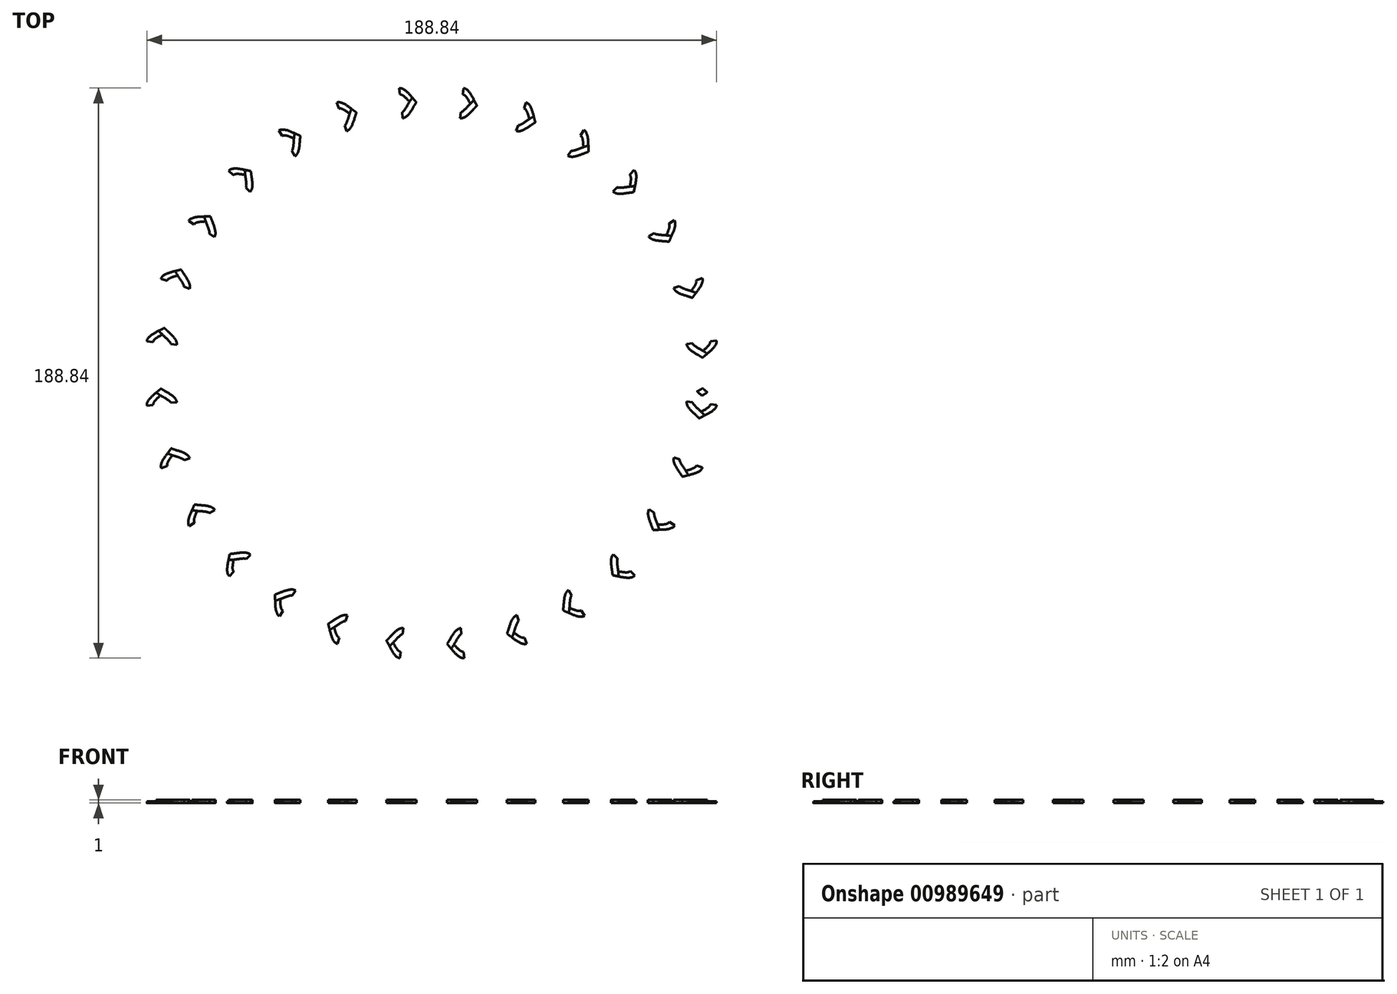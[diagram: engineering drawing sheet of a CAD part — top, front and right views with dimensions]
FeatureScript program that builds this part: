
annotation { "Feature Type Name" : "Feature", "Feature Type Description" : "" }
export const myFeature = defineFeature(function(context is Context, id is Id, definition is map)
    precondition{}
    {
        {
            var Q0;
            Q0=qCreatedBy(makeId("Top.planeOp"),FACE);
            var sketch = newSketch(context, id + "F0", { "sketchPlane" : qUnion([Q0])});
            skCircle(sketch, "E0", {"center": v(0, 0) * mm, "radius": 90 * mm, "construction": true});
            skLineSegment(sketch, "E1", {"start": v(0, 0) * mm, "end": v(90, 0) * mm, "construction": true});
            skLineSegment(sketch, "E2", {"start": v(89.42, 10.18) * mm, "end": v(90, 0) * mm, "construction": true});
            skLineSegment(sketch, "E3", {"start": v(0, 0) * mm, "end": v(89.42, 10.18) * mm, "construction": true});
            skLineSegment(sketch, "E4", {"start": v(90, 0) * mm, "end": v(89.44, -9.98) * mm, "construction": true});
            skLineSegment(sketch, "E5", {"start": v(0, 0) * mm, "end": v(89.44, -9.98) * mm, "construction": true});
            skLineSegment(sketch, "E6", {"start": v(90, 0) * mm, "end": v(85, 0) * mm});
            skLineSegment(sketch, "E7", {"start": v(85, 0) * mm, "end": v(87, 0) * mm});
            skLineSegment(sketch, "E8", {"start": v(90, 0) * mm, "end": v(95, 0) * mm});
            skLineSegment(sketch, "E9", {"start": v(95, 0) * mm, "end": v(93, 0) * mm});
            skLineSegment(sketch, "E10", {"start": v(89.42, 10.18) * mm, "end": v(84.45, 9.62) * mm});
            skLineSegment(sketch, "E11", {"start": v(84.45, 9.62) * mm, "end": v(86.44, 9.84) * mm});
            skLineSegment(sketch, "E12", {"start": v(86.44, 9.84) * mm, "end": v(86.67, 7.86) * mm, "construction": true});
            skLineSegment(sketch, "E13", {"start": v(84.45, 9.62) * mm, "end": v(84.68, 7.63) * mm, "construction": true});
            skLineSegment(sketch, "E14", {"start": v(89.42, 10.18) * mm, "end": v(94.39, 10.75) * mm});
            skLineSegment(sketch, "E15", {"start": v(94.39, 10.75) * mm, "end": v(92.28, 10.5) * mm});
            skLineSegment(sketch, "E16", {"start": v(92.28, 10.5) * mm, "end": v(92.5, 8.52) * mm, "construction": true});
            skLineSegment(sketch, "E17", {"start": v(94.39, 10.75) * mm, "end": v(94.62, 8.76) * mm, "construction": true});
            skLineSegment(sketch, "E18", {"start": v(87, 0) * mm, "end": v(87, 2) * mm, "construction": true});
            skLineSegment(sketch, "E19", {"start": v(93, 0) * mm, "end": v(93, 2) * mm, "construction": true});
            skLineSegment(sketch, "E20", {"start": v(90, 0) * mm, "end": v(89.71, 5.1) * mm, "construction": true});
            skFitSpline(sketch, "E21", {"points": [v(94.39, 10.75) * mm, v(89.71, 5.1) * mm, v(87, 0) * mm], "startDerivative": vector(1.28, -11.25) * mm, "endDerivative": vector(0, -12.77) * mm});
            skFitSpline(sketch, "E22", {"points": [v(84.45, 9.62) * mm, v(89.71, 5.1) * mm, v(93, 0) * mm], "startDerivative": vector(1.31, -11.53) * mm, "endDerivative": vector(0, -12.42) * mm});
            skFitSpline(sketch, "E23.0", {"points": [v(86.44, 9.84) * mm, v(86.44, 9.83) * mm, v(86.45, 9.8) * mm, v(86.56, 9.6) * mm, v(86.87, 9.27) * mm, v(87.4, 8.87) * mm, v(88.07, 8.43) * mm, v(88.86, 7.97) * mm, v(89.72, 7.47) * mm, v(90.46, 7) * mm, v(91.05, 6.6) * mm, v(91.63, 6.17) * mm, v(92.3, 5.6) * mm, v(93.04, 4.85) * mm, v(93.91, 3.76) * mm, v(94.74, 2.2) * mm, v(95, 0.74) * mm, v(95, 0) * mm]});
            skLineSegment(sketch, "E24", {"start": v(92.4, 10.52) * mm, "end": v(92.4, 10.5) * mm});
            skFitSpline(sketch, "E25", {"points": [v(85, 0) * mm, v(89.6, 7.15) * mm, v(92.28, 10.5) * mm], "startDerivative": vector(-0.2, 13.78) * mm, "endDerivative": vector(-0.82, 7.17) * mm});
            skLineSegment(sketch, "E26", {"start": v(89.44, -9.98) * mm, "end": v(84.48, -9.43) * mm});
            skLineSegment(sketch, "E27", {"start": v(84.48, -9.43) * mm, "end": v(86.46, -9.65) * mm});
            skLineSegment(sketch, "E28", {"start": v(86.46, -9.65) * mm, "end": v(86.68, -7.66) * mm, "construction": true});
            skLineSegment(sketch, "E29", {"start": v(84.48, -9.43) * mm, "end": v(84.7, -7.44) * mm, "construction": true});
            skLineSegment(sketch, "E30", {"start": v(89.44, -9.98) * mm, "end": v(94.41, -10.54) * mm});
            skLineSegment(sketch, "E31", {"start": v(94.41, -10.54) * mm, "end": v(92.43, -10.32) * mm});
            skLineSegment(sketch, "E32", {"start": v(92.43, -10.32) * mm, "end": v(92.43, -8.32) * mm, "construction": true});
            skLineSegment(sketch, "E33", {"start": v(94.41, -10.54) * mm, "end": v(94.41, -8.54) * mm, "construction": true});
            skLineSegment(sketch, "E34", {"start": v(87, 0) * mm, "end": v(87, -2) * mm, "construction": true});
            skLineSegment(sketch, "E35", {"start": v(93, 0) * mm, "end": v(93, -2) * mm, "construction": true});
            skLineSegment(sketch, "E36", {"start": v(90, 0) * mm, "end": v(89.72, -5) * mm});
            skFitSpline(sketch, "E37", {"points": [v(87, 0) * mm, v(89.72, -5) * mm, v(94.41, -10.54) * mm], "startDerivative": vector(0, -12.78) * mm, "endDerivative": vector(0, -11.3) * mm});
            skFitSpline(sketch, "E38", {"points": [v(93, 0) * mm, v(89.72, -5) * mm, v(84.48, -9.43) * mm], "startDerivative": vector(0, -12.44) * mm, "endDerivative": vector(-1.29, -11.52) * mm});
            skFitSpline(sketch, "E39.0", {"points": [v(85, 0) * mm, v(85, -0.71) * mm, v(85.15, -1.76) * mm, v(85.63, -3.02) * mm, v(86.1, -3.9) * mm, v(86.67, -4.7) * mm, v(87.3, -5.44) * mm, v(88, -6.13) * mm, v(88.75, -6.8) * mm, v(89.51, -7.45) * mm, v(90.25, -8.07) * mm, v(90.94, -8.66) * mm, v(91.54, -9.23) * mm, v(92, -9.75) * mm, v(92.3, -10.18) * mm, v(92.41, -10.46) * mm, v(92.41, -10.52) * mm, v(92.41, -10.54) * mm]});
            skFitSpline(sketch, "E40.0", {"points": [v(95, 0) * mm, v(95, -0.74) * mm, v(94.74, -2.2) * mm, v(93.9, -3.75) * mm, v(93.03, -4.82) * mm, v(92.28, -5.56) * mm, v(91.6, -6.11) * mm, v(91.03, -6.52) * mm, v(90.44, -6.92) * mm, v(89.7, -7.36) * mm, v(88.84, -7.85) * mm, v(88.06, -8.3) * mm, v(87.39, -8.72) * mm, v(86.88, -9.11) * mm, v(86.57, -9.43) * mm, v(86.47, -9.61) * mm, v(86.47, -9.63) * mm, v(86.46, -9.65) * mm]});
            skLineSegment(sketch, "E41", {"start": v(86.68, 9.48) * mm, "end": v(86.44, 9.84) * mm});
            skSolve(sketch);
        }
        {
            var Q0;
            {var subQ0=sQuery(id+"F0.wireOp",EDGE,"E9");Q0=makeQuery(id+"F0.imprint","IMPRINT",FACE,{"disambiguationData":[TD([[makeQuery(id+"F0.imprint","IMPRINT",EDGE,{"derivedFrom":subQ0}),-1.0]])]});}
            var Q1;
            {var subQ0=sQuery(id+"F0.wireOp",EDGE,"E23.0");var subQ1=sQuery(id+"F0.wireOp",EDGE,"E21");var subQ2=makeQuery(id+"F0.imprint","INTERSECT",VERTEX,{"derivedFrom":[subQ1,subQ0]});Q1=makeQuery(id+"F0.imprint","IMPRINT",FACE,{"disambiguationData":[TD([[makeQuery(id+"F0.imprint","IMPRINT",EDGE,{"disambiguationData":[TD([[subQ2,-1.0]])],"derivedFrom":subQ1}),-1.0]])]});}
            var Q2;
            {var subQ0=sQuery(id+"F0.wireOp",EDGE,"E11");Q2=makeQuery(id+"F0.imprint","IMPRINT",FACE,{"disambiguationData":[TD([[makeQuery(id+"F0.imprint","IMPRINT",EDGE,{"derivedFrom":subQ0}),-1.0]])]});}
            var Q3;
            {var subQ0=sQuery(id+"F0.wireOp",EDGE,"E9");Q3=makeQuery(id+"F0.imprint","IMPRINT",FACE,{"disambiguationData":[TD([[makeQuery(id+"F0.imprint","IMPRINT",EDGE,{"derivedFrom":subQ0}),1.0]])]});}
            var Q4;
            {var subQ0=sQuery(id+"F0.wireOp",EDGE,"E38");var subQ5=sQuery(id+"F0.wireOp",EDGE,"E39.0");var subQ6=makeQuery(id+"F0.imprint","INTERSECT",VERTEX,{"derivedFrom":[subQ0,subQ5]});Q4=makeQuery(id+"F0.imprint","IMPRINT",FACE,{"disambiguationData":[TD([[makeQuery(id+"F0.imprint","IMPRINT",EDGE,{"disambiguationData":[TD([[subQ6,-1.0]])],"derivedFrom":subQ5}),1.0]])]});}
            var Q5;
            {var subQ0=sQuery(id+"F0.wireOp",EDGE,"E27");Q5=makeQuery(id+"F0.imprint","IMPRINT",FACE,{"disambiguationData":[TD([[makeQuery(id+"F0.imprint","IMPRINT",EDGE,{"derivedFrom":subQ0}),1.0]])]});}
            extrude(context, id + "F1", {"entities" : qUnion([Q0, Q1, Q2, Q3, Q4, Q5]), "depth" : 1 * mm, "offsetDistance" : 25 * mm});
        }
        {
            var Q0;
            {var subQ0=sQuery(id+"F0.wireOp",EDGE,"E15");Q0=makeQuery(id+"F0.imprint","IMPRINT",FACE,{"disambiguationData":[TD([[makeQuery(id+"F0.imprint","IMPRINT",EDGE,{"derivedFrom":subQ0}),1.0]])]});}
            var Q1;
            {var subQ0=sQuery(id+"F0.wireOp",EDGE,"E7");Q1=makeQuery(id+"F0.imprint","IMPRINT",FACE,{"disambiguationData":[TD([[makeQuery(id+"F0.imprint","IMPRINT",EDGE,{"derivedFrom":subQ0}),1.0]])]});}
            var Q2;
            {var subQ0=sQuery(id+"F0.wireOp",EDGE,"E7");Q2=makeQuery(id+"F0.imprint","IMPRINT",FACE,{"disambiguationData":[TD([[makeQuery(id+"F0.imprint","IMPRINT",EDGE,{"derivedFrom":subQ0}),-1.0]])]});}
            var Q3;
            {var subQ5=sQuery(id+"F0.wireOp",EDGE,"E31");Q3=makeQuery(id+"F0.imprint","IMPRINT",FACE,{"disambiguationData":[TD([[makeQuery(id+"F0.imprint","IMPRINT",EDGE,{"derivedFrom":subQ5}),-1.0]])]});}
            extrude(context, id + "F2", {"entities" : qUnion([Q0, Q1, Q2, Q3]), "operationType" : NewBodyOperationType.ADD, "depth" : 0.5 * mm, "offsetDistance" : 25 * mm});
        }
        {
            var Q0;
            Q0=qCreatedBy(makeId("Right.planeOp"),FACE);
            var sketch = newSketch(context, id + "F3", { "sketchPlane" : qUnion([Q0])});
            skLineSegment(sketch, "E42", {"start": v(0, 0) * mm, "end": v(0, 4.2) * mm, "construction": true});
            skSolve(sketch);
        }
        {
            var Q0;
            Q0=makeQuery(id+"F1.opExtrude","SWEPT_BODY",BODY,{"disambiguationData":[OSD([sQuery(id+"F0.wireOp",EDGE,"E11"),sQuery(id+"F0.wireOp",EDGE,"E22"),sQuery(id+"F0.wireOp",EDGE,"E23.0"),sQuery(id+"F0.wireOp",EDGE,"E27"),sQuery(id+"F0.wireOp",EDGE,"E38"),sQuery(id+"F0.wireOp",EDGE,"E40.0")])]});
            var Q1;
            Q1=sQuery(id+"F3.wireOp",EDGE,"E42");
            circularPattern(context, id + "F4", {"operationType" : NewBodyOperationType.ADD, "entities" : qUnion([Q0]), "axis" : qUnion([Q1]), "angle" : 360 * degree, "instanceCount" : 28, "equalSpace" : true});
        }
    });
